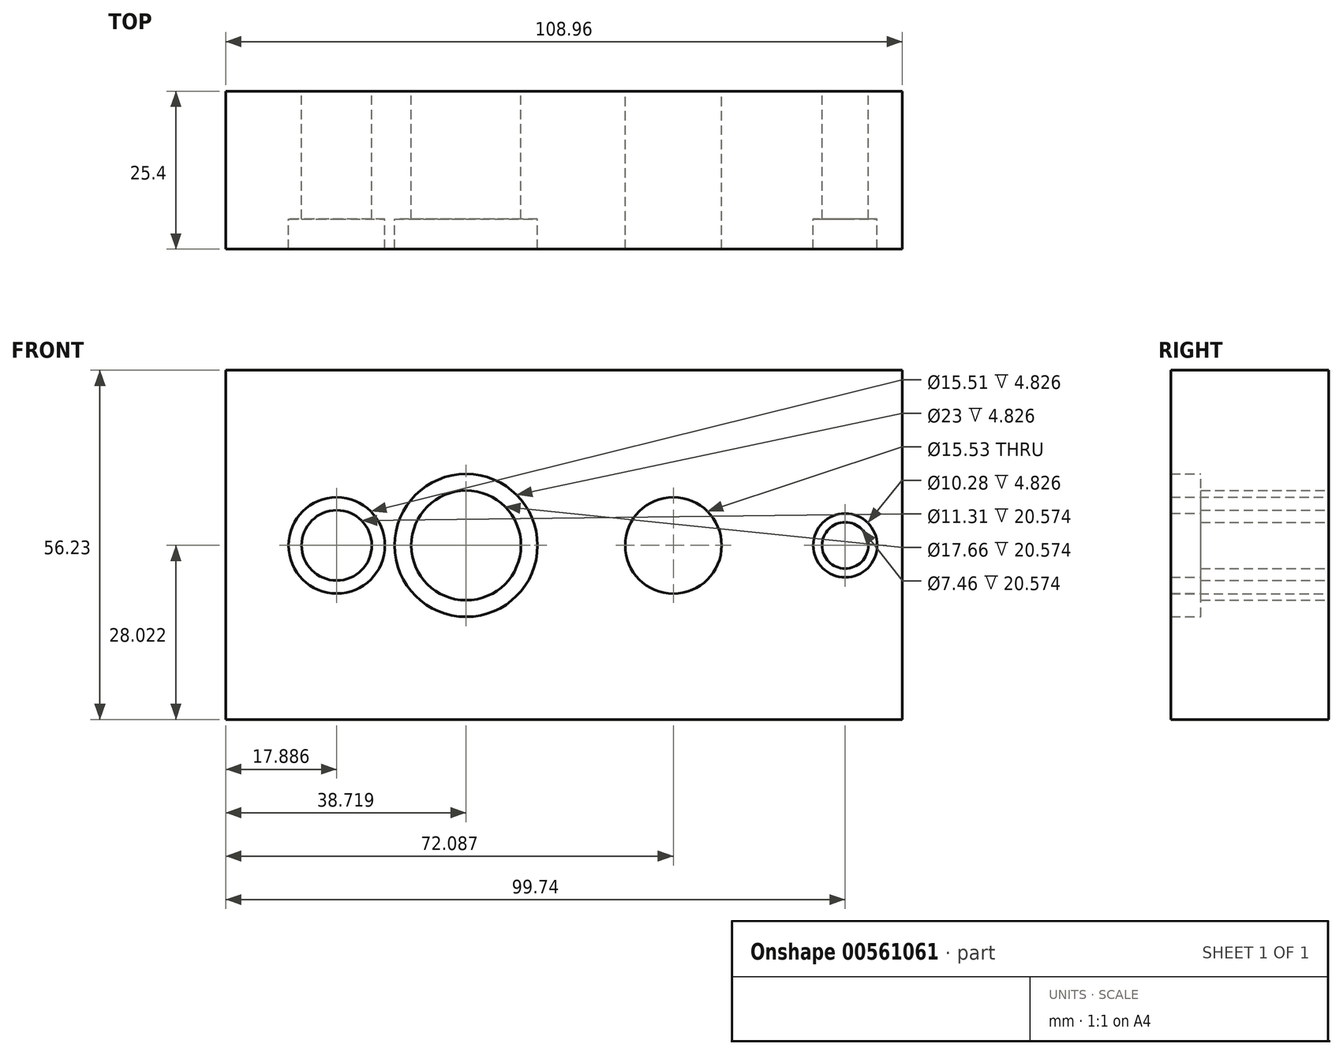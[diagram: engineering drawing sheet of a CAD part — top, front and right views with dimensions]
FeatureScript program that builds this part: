
annotation { "Feature Type Name" : "Feature", "Feature Type Description" : "" }
export const myFeature = defineFeature(function(context is Context, id is Id, definition is map)
    precondition{}
    {
        {
            var Q0;
            Q0=qCreatedBy(makeId("Front.planeOp"),FACE);
            var sketch = newSketch(context, id + "F0", { "sketchPlane" : qUnion([Q0])});
            skLineSegment(sketch, "E0.bottom", {"start": v(-54.02, 33.37) * mm, "end": v(54.94, 33.37) * mm});
            skLineSegment(sketch, "E0.top", {"start": v(-54.02, -22.86) * mm, "end": v(54.94, -22.86) * mm});
            skLineSegment(sketch, "E0.left", {"start": v(-54.02, 33.37) * mm, "end": v(-54.02, -22.86) * mm});
            skLineSegment(sketch, "E0.right", {"start": v(54.94, 33.37) * mm, "end": v(54.94, -22.86) * mm});
            skCircle(sketch, "E1", {"center": v(-36.13, 5.16) * mm, "radius": 7.75 * mm});
            skCircle(sketch, "E2", {"center": v(-36.13, 5.16) * mm, "radius": 5.66 * mm});
            skCircle(sketch, "E3", {"center": v(-15.3, 5.16) * mm, "radius": 11.5 * mm});
            skCircle(sketch, "E4", {"center": v(-15.3, 5.16) * mm, "radius": 8.83 * mm});
            skCircle(sketch, "E5", {"center": v(18.07, 5.16) * mm, "radius": 7.76 * mm});
            skCircle(sketch, "E6", {"center": v(45.72, 5.16) * mm, "radius": 5.14 * mm});
            skCircle(sketch, "E7", {"center": v(45.72, 5.16) * mm, "radius": 3.73 * mm});
            skSolve(sketch);
        }
        {
            var Q0;
            Q0=makeQuery(id+"F0.imprint","IMPRINT",FACE,{"disambiguationData":[TD([[makeQuery(id+"F0.imprint","IMPRINT",EDGE,{"derivedFrom":sQuery(id+"F0.wireOp",EDGE,"E0.bottom")}),-1.0]])]});
            extrude(context, id + "F1", {"entities" : qUnion([Q0]), "depth" : 25.4 * mm, "offsetDistance" : 25.4 * mm});
        }
        {
            var Q0;
            Q0=makeQuery(id+"F0.imprint","IMPRINT",FACE,{"disambiguationData":[TD([[makeQuery(id+"F0.imprint","IMPRINT",EDGE,{"derivedFrom":sQuery(id+"F0.wireOp",EDGE,"E1")}),1.0]])]});
            var Q1;
            Q1=makeQuery(id+"F0.imprint","IMPRINT",FACE,{"disambiguationData":[TD([[makeQuery(id+"F0.imprint","IMPRINT",EDGE,{"derivedFrom":sQuery(id+"F0.wireOp",EDGE,"E6")}),1.0]])]});
            var Q2;
            Q2=makeQuery(id+"F0.imprint","IMPRINT",FACE,{"disambiguationData":[TD([[makeQuery(id+"F0.imprint","IMPRINT",EDGE,{"derivedFrom":sQuery(id+"F0.wireOp",EDGE,"E3")}),1.0]])]});
            extrude(context, id + "F2", {"entities" : qUnion([Q0, Q1, Q2]), "operationType" : NewBodyOperationType.ADD, "depth" : 20.57 * mm, "offsetDistance" : 25.4 * mm});
        }
    });
